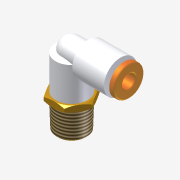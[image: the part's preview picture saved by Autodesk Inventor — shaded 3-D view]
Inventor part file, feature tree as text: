
AUTODESK INVENTOR PART (.ipt)
format: ipt  version: unknown  size: 266,240 bytes
history: native  units: mm
features: imported_body x1, thread x1
ambient origin geometry x8: Origin, YZ Plane, XZ Plane, XY Plane, X Axis, Y Axis, Z Axis, Center Point
feature tree (2):
  imported_body  "Base1"
  thread  "Thread1"  [1 undecoded]
note: 1 required parameter value undecoded (feature->parameter linkage not recoverable at this tier; creation-order binding heuristic only, values carry confidence <= 0.55)
